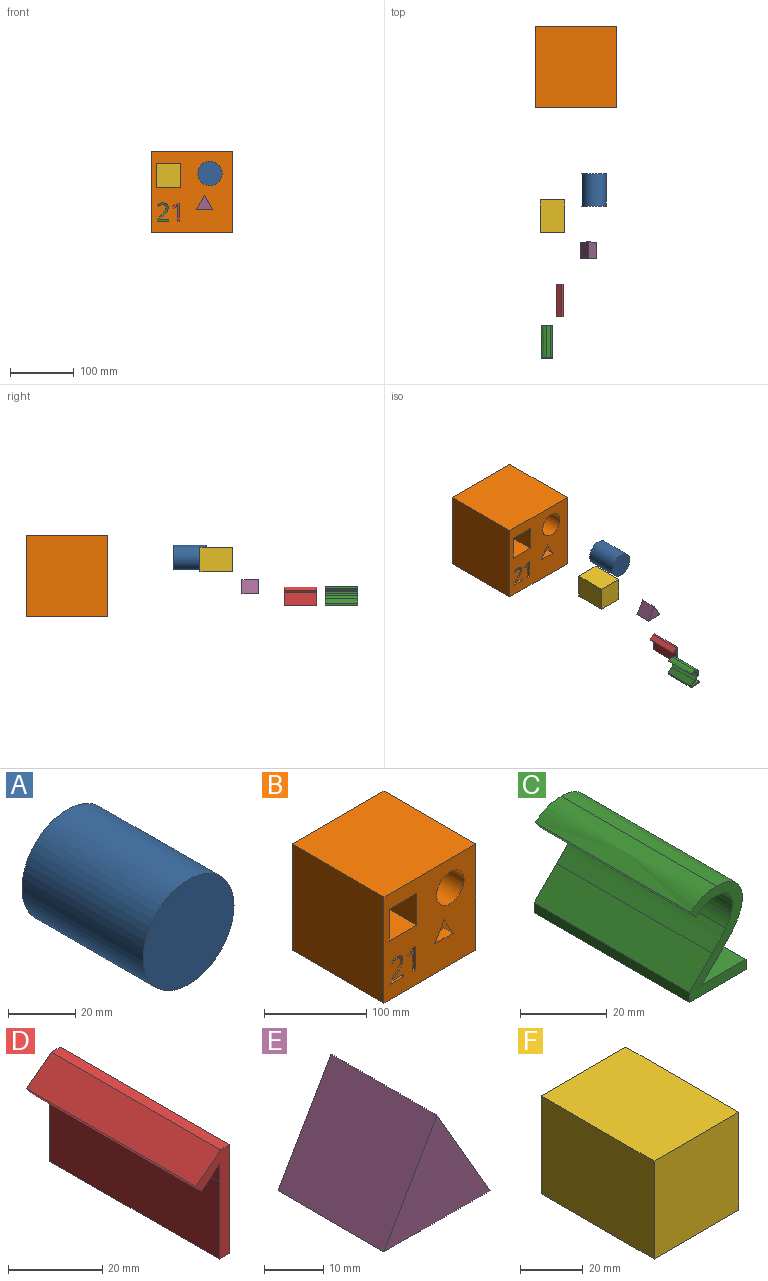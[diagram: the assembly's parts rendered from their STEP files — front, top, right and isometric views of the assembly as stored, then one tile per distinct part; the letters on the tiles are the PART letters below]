
ASSEMBLY  parts=6 mates=5
PART A: 3 faces, bbox 38.1x50.8x38.1 mm
  f0: cylinder r=19.05mm len=50.8mm, axis (0,1,0), area 6080.5mm2, adj f1,f2
  f1: plane 38.1x38.1mm, normal (0,-1,0), area 1140.1mm2, adj f0
  f2: plane 38.1x38.1mm, normal (0,1,0), area 1140.1mm2, adj f0
PART B: 48 faces, bbox 127x127x127 mm
  f0: plane 127x127mm, normal (0,-1,0), area 12975.1mm2, adj f1,f2,f3,f4,f6,f7,f8,f9
  f1: plane 127x127mm, normal (-1,0,0), area 16129mm2, adj f0,f2,f4,f5
  f2: plane 127x127mm, normal (0,0,-1), area 16129mm2, adj f0,f1,f3,f5
  f3: plane 127x127mm, normal (1,0,0), area 16129mm2, adj f0,f2,f4,f5
  f4: plane 127x127mm, normal (0,0,1), area 16129mm2, adj f0,f1,f3,f5
  f5: plane 127x127mm, normal (0,1,0), area 16129mm2, adj f1,f2,f3,f4
  f6: plane 50.8x38.1mm, normal (1,0,0), area 1935.5mm2, adj f0,f7,f9,f10
  f7: plane 50.8x38.1mm, normal (0,0,1), area 1935.5mm2, adj f0,f6,f8,f10
  f8: plane 50.8x38.1mm, normal (-1,0,0), area 1935.5mm2, adj f0,f7,f9,f10
  f9: plane 50.8x38.1mm, normal (0,0,-1), area 1935.5mm2, adj f0,f6,f8,f10
  f10: plane 38.1x38.1mm, normal (0,-1,0), area 1451.6mm2, adj f6,f7,f8,f9
  f11: cylinder r=19.05mm len=38.1mm, axis (0,-1,0), area 4560.4mm2, adj f0,f12
  f12: plane 38.1x38.1mm, normal (0,-1,0), area 1140.1mm2, adj f11
  f13: plane 28.14x12.7mm, normal (-1,0,0), area 357.4mm2, adj f0,f14,f21,f22
  f14: plane 12.7x2.69mm, normal (0,0,-1), area 34.2mm2, adj f0,f13,f15,f22
  f15: plane 12.7x7.45mm, normal (0.61,0,-0.79), area 119.5mm2, adj f0,f14,f16,f22
  f16: plane 12.7x2.19mm, normal (0.79,0,0.61), area 35.2mm2, adj f0,f15,f17,f22
  f17: extruded ~12.7x4.58mm, area 75.2mm2, adj f0,f16,f18,f22
  f18: extruded ~12.7x0.9mm, area 15.7mm2, adj f0,f17,f19,f22
  f19: extruded ~12.7x4.74mm, area 60.2mm2, adj f0,f18,f20,f22
  f20: plane 20.05x12.7mm, normal (1,0,0), area 254.7mm2, adj f0,f19,f21,f22
  f21: plane 12.7x3.12mm, normal (0,0,1), area 39.6mm2, adj f0,f13,f20,f22
  f22: plane 28.14x10.14mm, normal (0,-1,0), area 108.4mm2, adj f13,f14,f15,f16,f17,f18,f19,f20
  f23: plane 12.7x2.96mm, normal (-1,0,0), area 37.6mm2, adj f0,f24,f42,f43
  f24: plane 14.47x12.7mm, normal (0,0,-1), area 183.8mm2, adj f0,f23,f25,f43
  f25: plane 12.7x0.15mm, normal (-1,0,0), area 2mm2, adj f0,f24,f26,f43
  f26: plane 12.7x6.16mm, normal (-0.7,0,0.71), area 109.4mm2, adj f0,f25,f27,f43
  f27: extruded ~12.7x6.62mm, area 110.6mm2, adj f0,f26,f28,f43
  f28: extruded ~12.7x5.3mm, area 70.7mm2, adj f0,f27,f29,f43
  f29: extruded ~12.7x5.45mm, area 77.3mm2, adj f0,f28,f30,f43
  f30: extruded ~12.7x6.22mm, area 85mm2, adj f0,f29,f31,f43
  f31: extruded ~12.7x8.47mm, area 117.6mm2, adj f0,f30,f32,f43
  f32: plane 12.7x2.17mm, normal (0.79,0,0.61), area 35mm2, adj f0,f31,f33,f43
  f33: extruded ~12.7x3.49mm, area 52mm2, adj f0,f32,f34,f43
  f34: extruded ~12.7x3.32mm, area 43mm2, adj f0,f33,f35,f43
  f35: extruded ~12.7x3.79mm, area 52.3mm2, adj f0,f34,f36,f43
  f36: extruded ~12.7x3.57mm, area 50mm2, adj f0,f35,f37,f43
  f37: extruded ~12.7x2.98mm, area 38.7mm2, adj f0,f36,f38,f43
  f38: extruded ~12.7x2.85mm, area 41.7mm2, adj f0,f37,f39,f43
  f39: extruded ~12.7x4.89mm, area 84.2mm2, adj f0,f38,f40,f43
  f40: plane 12.7x7.45mm, normal (0.71,0,-0.71), area 133.4mm2, adj f0,f39,f41,f43
  f41: plane 12.7x2.75mm, normal (1,0,0), area 35mm2, adj f0,f40,f42,f43
  f42: plane 18.49x12.7mm, normal (0,0,1), area 234.9mm2, adj f0,f23,f41,f43
  f43: plane 28.54x18.49mm, normal (0,-1,0), area 174.5mm2, adj f23,f24,f25,f26,f27,f28,f29,f30
  f44: plane 22.14x12.7mm, normal (-0.87,0,-0.49), area 322.6mm2, adj f0,f45,f46,f47
  f45: plane 21.85x12.95mm, normal (0.86,0,-0.51), area 322.6mm2, adj f0,f44,f46,f47
  f46: plane 25.4x12.7mm, normal (0.01,0,1), area 322.6mm2, adj f0,f44,f45,f47
  f47: plane 25.4x22.14mm, normal (0,-1,0), area 279.4mm2, adj f44,f45,f46
PART C: 22 faces, bbox 18.5x50.8x28.5 mm
  f0: plane 50.8x2.96mm, normal (1,0,0), area 150.5mm2, adj f1,f19,f20,f21
  f1: plane 50.8x14.47mm, normal (0,0,1), area 735.2mm2, adj f0,f2,f20,f21
  f2: plane 50.8x0.15mm, normal (1,0,0), area 7.8mm2, adj f1,f3,f20,f21
  f3: plane 50.8x6.16mm, normal (0.7,0,-0.71), area 437.6mm2, adj f2,f4,f20,f21
  f4: extruded ~50.8x6.62mm, area 442.3mm2, adj f3,f5,f20,f21
  f5: extruded ~50.8x5.3mm, area 282.9mm2, adj f4,f6,f20,f21
  f6: extruded ~50.8x5.45mm, area 309.3mm2, adj f5,f7,f20,f21
  f7: extruded ~50.8x6.22mm, area 340mm2, adj f6,f8,f20,f21
  f8: extruded ~50.8x8.47mm, area 470.3mm2, adj f7,f9,f20,f21
  f9: plane 50.8x2.17mm, normal (-0.79,0,-0.61), area 140mm2, adj f8,f10,f20,f21
  f10: extruded ~50.8x3.49mm, area 207.8mm2, adj f9,f11,f20,f21
  f11: extruded ~50.8x3.32mm, area 172.1mm2, adj f10,f12,f20,f21
  f12: extruded ~50.8x3.79mm, area 209.3mm2, adj f11,f13,f20,f21
  f13: extruded ~50.8x3.57mm, area 199.9mm2, adj f12,f14,f20,f21
  f14: extruded ~50.8x2.98mm, area 154.8mm2, adj f13,f15,f20,f21
  f15: extruded ~50.8x2.85mm, area 166.9mm2, adj f14,f16,f20,f21
  f16: extruded ~50.8x4.89mm, area 336.7mm2, adj f15,f17,f20,f21
  f17: plane 50.8x7.45mm, normal (-0.71,0,0.71), area 533.6mm2, adj f16,f18,f20,f21
  f18: plane 50.8x2.75mm, normal (-1,0,0), area 139.9mm2, adj f17,f19,f20,f21
  f19: plane 50.8x18.49mm, normal (0,0,-1), area 939.5mm2, adj f0,f18,f20,f21
  f20: plane 28.54x18.49mm, normal (0,-1,0), area 174.5mm2, adj f0,f1,f2,f3,f4,f5,f6,f7
  f21: plane 28.54x18.49mm, normal (0,1,0), area 174.5mm2, adj f0,f1,f2,f3,f4,f5,f6,f7
PART D: 11 faces, bbox 10.1x50.8x28.1 mm
  f0: plane 50.8x28.14mm, normal (1,0,0), area 1429.5mm2, adj f1,f8,f9,f10
  f1: plane 50.8x2.69mm, normal (0,0,1), area 136.7mm2, adj f0,f2,f9,f10
  f2: plane 50.8x7.45mm, normal (-0.61,0,0.79), area 478.2mm2, adj f1,f3,f9,f10
  f3: plane 50.8x2.19mm, normal (-0.79,0,-0.61), area 140.7mm2, adj f2,f4,f9,f10
  f4: extruded ~50.8x4.58mm, area 300.8mm2, adj f3,f5,f9,f10
  f5: extruded ~50.8x0.9mm, area 62.9mm2, adj f4,f6,f9,f10
  f6: extruded ~50.8x4.74mm, area 240.8mm2, adj f5,f7,f9,f10
  f7: plane 50.8x20.05mm, normal (-1,0,0), area 1018.7mm2, adj f6,f8,f9,f10
  f8: plane 50.8x3.12mm, normal (0,0,-1), area 158.3mm2, adj f0,f7,f9,f10
  f9: plane 28.14x10.14mm, normal (0,-1,0), area 108.4mm2, adj f0,f1,f2,f3,f4,f5,f6,f7
  f10: plane 28.14x10.14mm, normal (0,1,0), area 108.4mm2, adj f0,f1,f2,f3,f4,f5,f6,f7
PART E: 5 faces, bbox 25.4x25.4x22 mm
  f0: plane 25.4x25.4mm, normal (0,0,-1), area 645.2mm2, adj f1,f2,f3,f4
  f1: plane 25.4x22mm, normal (0.87,0,0.5), area 645.2mm2, adj f0,f2,f3,f4
  f2: plane 25.4x22mm, normal (-0.87,0,0.5), area 645.2mm2, adj f0,f1,f3,f4
  f3: plane 25.4x22mm, normal (0,-1,0), area 279.4mm2, adj f0,f1,f2
  f4: plane 25.4x22mm, normal (0,1,0), area 279.4mm2, adj f0,f1,f2
PART F: 6 faces, bbox 38.1x50.8x38.1 mm
  f0: plane 50.8x38.1mm, normal (-1,0,0), area 1935.5mm2, adj f1,f3,f4,f5
  f1: plane 50.8x38.1mm, normal (0,0,-1), area 1935.5mm2, adj f0,f2,f4,f5
  f2: plane 50.8x38.1mm, normal (1,0,0), area 1935.5mm2, adj f1,f3,f4,f5
  f3: plane 50.8x38.1mm, normal (0,0,1), area 1935.5mm2, adj f0,f2,f4,f5
  f4: plane 38.1x38.1mm, normal (0,-1,0), area 1451.6mm2, adj f0,f1,f2,f3
  f5: plane 38.1x38.1mm, normal (0,1,0), area 1451.6mm2, adj f0,f1,f2,f3
PLACE A t=(178.72,-167.46,15.22)mm
PLACE B at identity fixed
PLACE C t=(80.32,-405.14,-89.22)mm
PLACE D t=(80.32,-340.67,-89.22)mm
PLACE E t=(115.11,-274.44,-12.4)mm
PLACE F t=(65.81,-208.71,63.13)mm
MATE slider F.f5 <-> B.f10  axis (0,1,0) through (-25.06,-208.71,28.45)mm
MATE slider A.f0 <-> B.f11  axis (0,1,0) through (40.19,-167.46,31.34)mm
MATE slider D.f10 <-> B.f0  axis (0,1,0) through (-8.29,-340.67,-29.16)mm
MATE slider C.f21 <-> B.f0  axis (0,1,0) through (-30.78,-405.14,-28.14)mm
MATE slider E.f4 <-> B.f0  axis (0,1,0) through (25.22,-274.44,-14.14)mm
